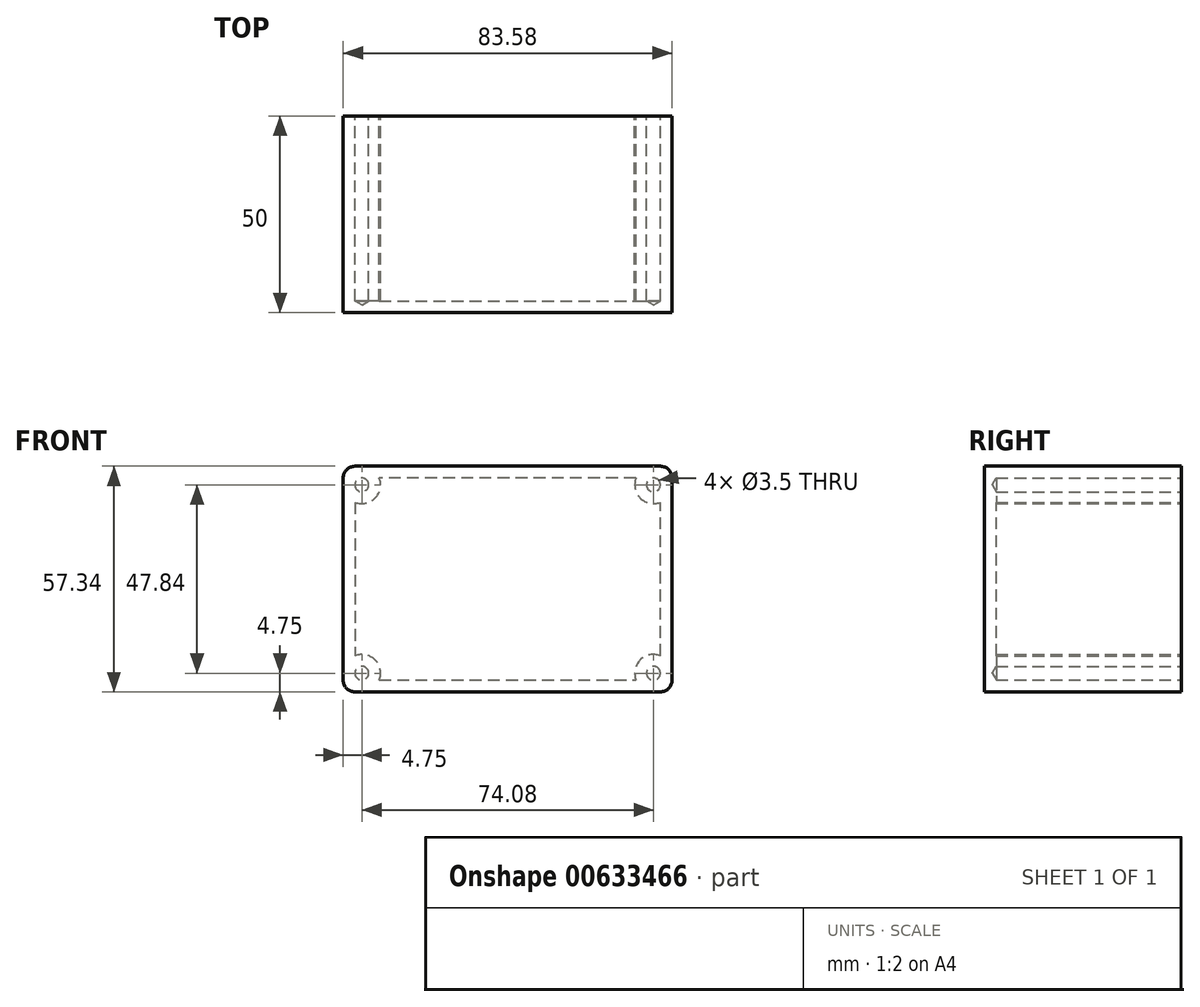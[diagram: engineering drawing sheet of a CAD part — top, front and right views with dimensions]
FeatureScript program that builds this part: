
annotation { "Feature Type Name" : "Feature", "Feature Type Description" : "" }
export const myFeature = defineFeature(function(context is Context, id is Id, definition is map)
    precondition{}
    {
        {
            var Q0;
            Q0=qCreatedBy(makeId("Front.planeOp"),FACE);
            var sketch = newSketch(context, id + "F0", { "sketchPlane" : qUnion([Q0])});
            skLineSegment(sketch, "E0", {"start": v(0, 0) * mm, "end": v(83.58, 0) * mm});
            skLineSegment(sketch, "E1", {"start": v(83.58, 0) * mm, "end": v(83.58, 57.34) * mm});
            skLineSegment(sketch, "E2", {"start": v(83.58, 57.34) * mm, "end": v(0, 57.34) * mm});
            skLineSegment(sketch, "E3", {"start": v(0, 57.34) * mm, "end": v(0, 0) * mm});
            skSolve(sketch);
        }
        {
            var Q0;
            Q0=makeQuery(id+"F0.imprint","IMPRINT",FACE,{"disambiguationData":[TD([[makeQuery(id+"F0.imprint","IMPRINT",EDGE,{"derivedFrom":sQuery(id+"F0.wireOp",EDGE,"E0")}),1.0]])]});
            extrude(context, id + "F1", {"entities" : qUnion([Q0]), "depth" : 50 * mm, "offsetDistance" : 25.4 * mm});
        }
        {
            var Q0;
            Q0=qCreatedBy(makeId("Front.planeOp"),FACE);
            var sketch = newSketch(context, id + "F2", { "sketchPlane" : qUnion([Q0])});
            skCircle(sketch, "E4", {"center": v(4.75, 52.6) * mm, "radius": 1.75 * mm});
            skCircle(sketch, "E5", {"center": v(78.83, 52.6) * mm, "radius": 1.75 * mm});
            skCircle(sketch, "E6", {"center": v(78.83, 4.75) * mm, "radius": 1.75 * mm});
            skCircle(sketch, "E7", {"center": v(4.75, 4.75) * mm, "radius": 1.75 * mm});
            skSolve(sketch);
        }
        {
            var Q0;
            Q0=sQuery(id+"F2.wireOp",VERTEX,"E6.center");
            var Q1;
            Q1=sQuery(id+"F2.wireOp",VERTEX,"E5.center");
            var Q2;
            Q2=sQuery(id+"F2.wireOp",VERTEX,"E7.center");
            var Q3;
            Q3=sQuery(id+"F2.wireOp",VERTEX,"E4.center");
            var Q4;
            Q4=makeQuery(id+"F1.opExtrude","SWEPT_BODY",BODY,{"disambiguationData":[OSD([sQuery(id+"F0.wireOp",EDGE,"E0"),sQuery(id+"F0.wireOp",EDGE,"E1"),sQuery(id+"F0.wireOp",EDGE,"E2"),sQuery(id+"F0.wireOp",EDGE,"E3")])]});
            hole(context, id + "F3", {"style" : HoleStyle.SIMPLE, "endStyle" : HoleEndStyle.BLIND, "oppositeDirection" : true, "holeDiameter" : 3.5 * mm, "majorDiameter" : 6.35 * mm, "holeDepth" : 47 * mm, "isTappedThrough" : true, "tappedDepth" : 12.7 * mm, "tapClearance" : 3, "startFromSketch" : true, "locations" : qUnion([Q0, Q1, Q2, Q3]), "scope" : qUnion([Q4])});
        }
        {
            var Q0;
            Q0=makeQuery(id+"F1.opExtrude","CAP_FACE",FACE,{"disambiguationData":[OSD([sQuery(id+"F0.wireOp",EDGE,"E0"),sQuery(id+"F0.wireOp",EDGE,"E1"),sQuery(id+"F0.wireOp",EDGE,"E2"),sQuery(id+"F0.wireOp",EDGE,"E3")])],"isStart":true});
            shell(context, id + "F4", {"entities" : qUnion([Q0]), "thickness" : 3 * mm});
        }
        {
            var Q0;
            Q0=makeQuery(id+"F1.opExtrude","SWEPT_EDGE",EDGE,{"disambiguationData":[OSD([sQuery(id+"F0.wireOp",EDGE,"E2"),sQuery(id+"F0.wireOp",EDGE,"E3")])]});
            var Q1;
            Q1=makeQuery(id+"F1.opExtrude","SWEPT_EDGE",EDGE,{"disambiguationData":[OSD([sQuery(id+"F0.wireOp",EDGE,"E0"),sQuery(id+"F0.wireOp",EDGE,"E3")])]});
            var Q2;
            Q2=makeQuery(id+"F1.opExtrude","SWEPT_EDGE",EDGE,{"disambiguationData":[OSD([sQuery(id+"F0.wireOp",EDGE,"E1"),sQuery(id+"F0.wireOp",EDGE,"E2")])]});
            var Q3;
            Q3=makeQuery(id+"F1.opExtrude","SWEPT_EDGE",EDGE,{"disambiguationData":[OSD([sQuery(id+"F0.wireOp",EDGE,"E0"),sQuery(id+"F0.wireOp",EDGE,"E1")])]});
            fillet(context, id + "F5", {"entities" : qUnion([Q0, Q1, Q2, Q3]), "radius" : 3 * mm, "tangentPropagation" : true, "allowEdgeOverflow" : false});
        }
    });
